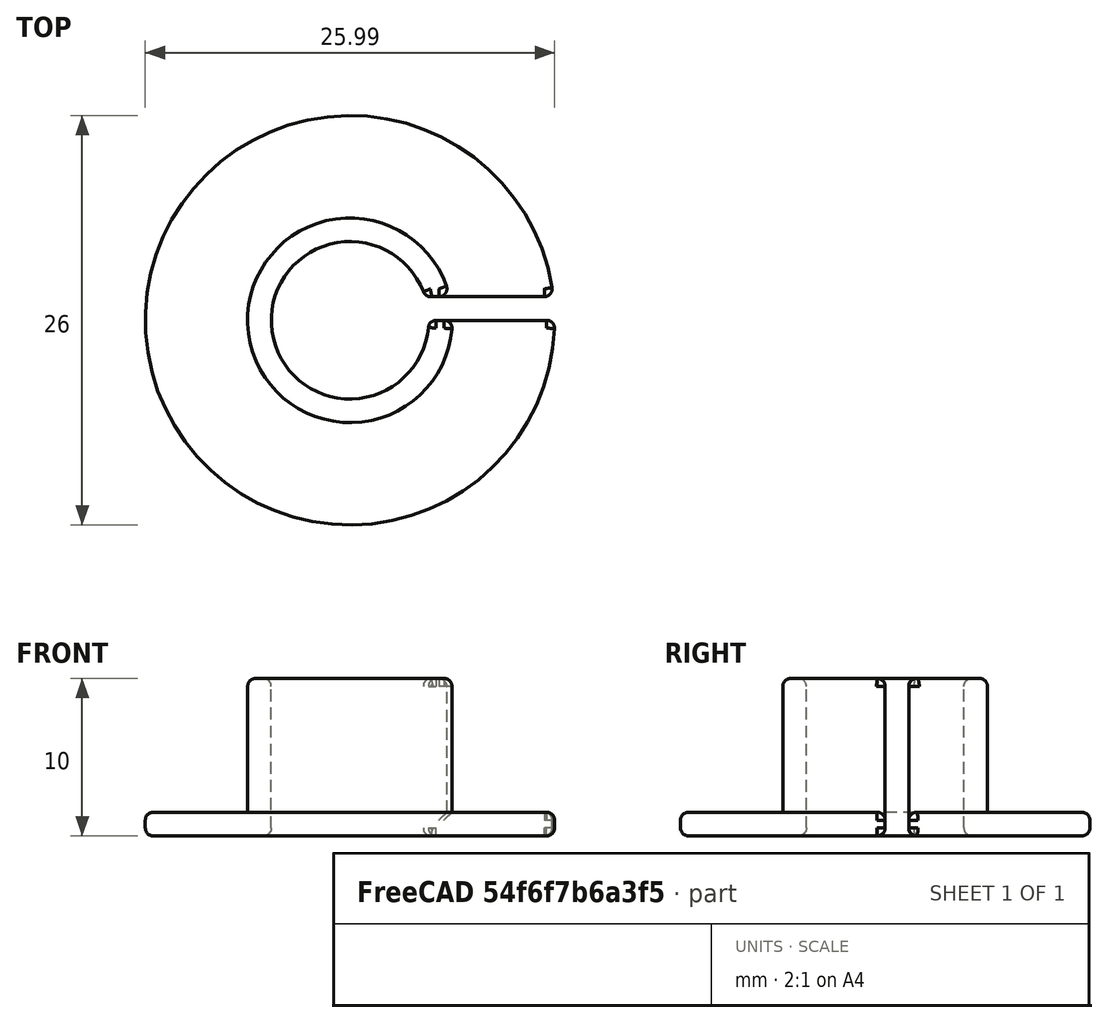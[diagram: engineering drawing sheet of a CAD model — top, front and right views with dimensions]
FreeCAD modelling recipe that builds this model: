
FCSTD DOCUMENT  (FreeCAD 0.16R6712 (Git))
Label: penCollar
License: All rights reserved
LicenseURL: http://en.wikipedia.org/wiki/All_rights_reserved
objects: PartDesign::Fillet×6, Part::Cylinder×3, Part::MultiFuse×2, Sketcher::SketchObject×1, Spreadsheet::Sheet×1, Part::Box×1, Part::Cut×1
note: 14 computed .brp shape members not serialized (recipe doc carries the construction recipe); baked Part::Feature solids carry a one-line shape summary decoded from their .brp

FEATURE [Sketcher::SketchObject] Sketch
FEATURE [Part::Cylinder] Cylinder  label="hatBase"
  Angle = 360
  Height = 1.5
  Radius = 13
  expr: Height = data.wallWidth
  expr: Radius = data.hatDiameter / 2
FEATURE [Part::Cylinder] Cylinder001  label="hatBody"
  Angle = 360
  Height = 10
  Radius = 6.5
  expr: Radius = data.penDiameter / 2 + data.wallWidth
  expr: Height = data.hatHeight
FEATURE [Spreadsheet::Sheet] Spreadsheet  label="data"
  cells = A3=penDiameter; B3(penDiameter)==10mm; A4=penRadius; B4==data.penDiameter / 2; A5=wallWidth; B5(wallWidth)==1.5mm; A6=hatDiameter; B6(hatDiameter)==26mm; A7=hatRadius; B7==data.hatDiameter / 2; A8=hatHeight; B8(hatHeight)==10mm
FEATURE [Part::Cylinder] Cylinder002  label="bore"
  Angle = 360
  Height = 11
  Radius = 5
  expr: Height = data.hatHeight + 1mm
  expr: Radius = data.penDiameter / 2
FEATURE [Part::Box] Box  label="slice"
  Height = 10
  Length = 13
  Width = 1.5
  expr: Length = data.hatDiameter / 2
  expr: Width = data.wallWidth
FEATURE [Part::MultiFuse] Fusion  label="body"
  Shapes = -> [Cylinder,Cylinder001]
FEATURE [Part::MultiFuse] Fusion001  label="cut"
  Shapes = -> [Box,Cylinder002]
FEATURE [Part::Cut] Cut
  Base = -> Fusion
  Tool = -> Fusion001
FEATURE [PartDesign::Fillet] Fillet
  Base = -> Cut [Edge21,Edge19]
  Radius = 0.5
FEATURE [PartDesign::Fillet] Fillet001
  Base = -> Fillet [Edge20]
  Radius = 0.5
FEATURE [PartDesign::Fillet] Fillet002
  Base = -> Fillet001 [Edge12]
  Radius = 0.5
FEATURE [PartDesign::Fillet] Fillet003
  Base = -> Fillet002 [Edge26]
  Radius = 0.5
FEATURE [PartDesign::Fillet] Fillet004
  Base = -> Fillet003 [Edge13]
  Radius = 0.5
FEATURE [PartDesign::Fillet] Fillet005
  Base = -> Fillet004 [Edge3]
  Radius = 0.5
